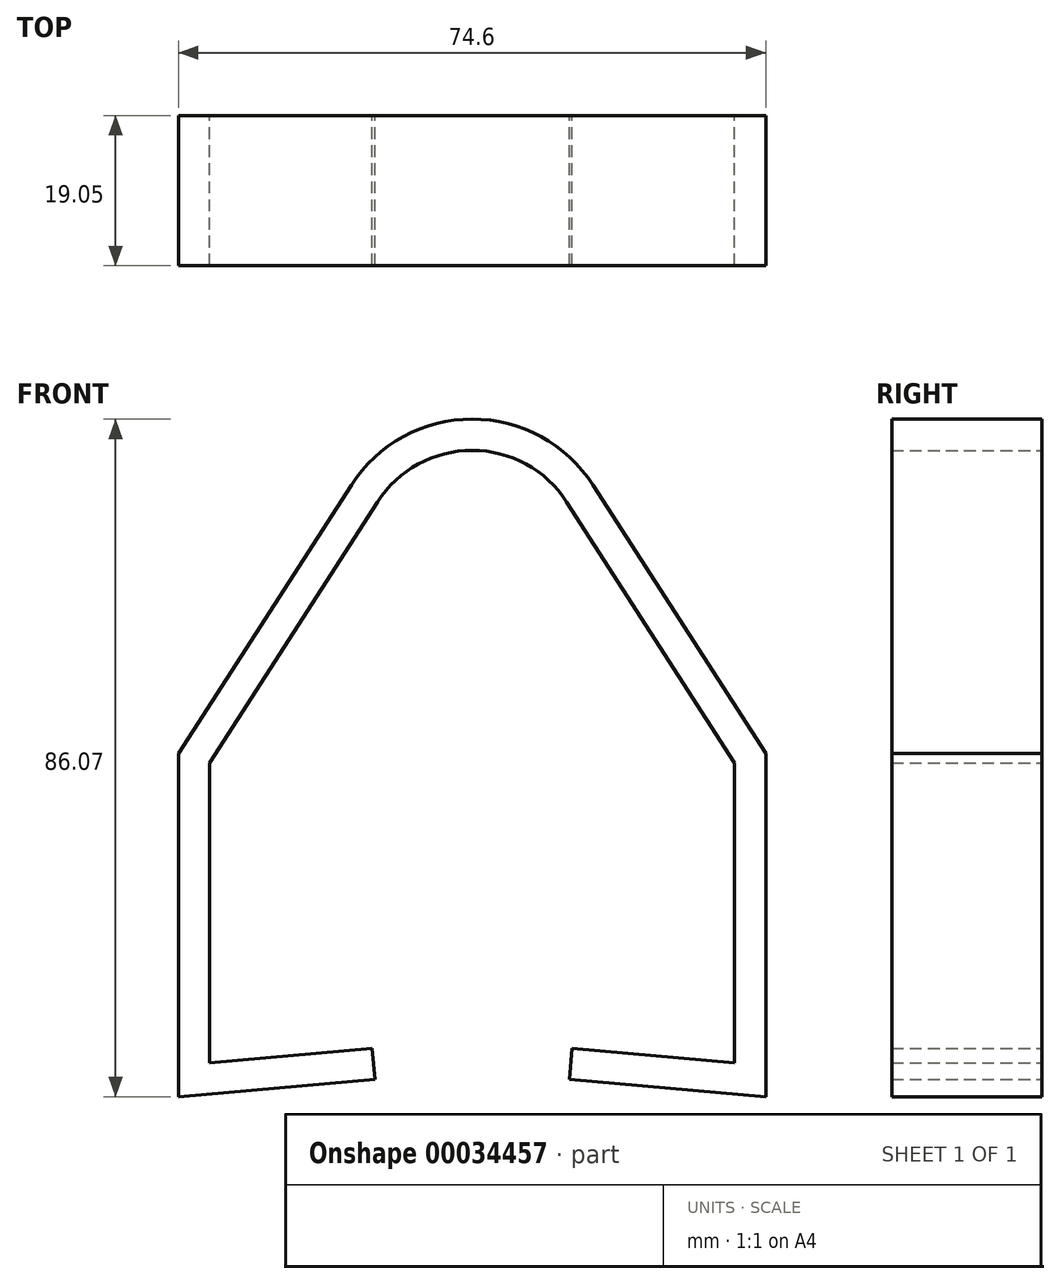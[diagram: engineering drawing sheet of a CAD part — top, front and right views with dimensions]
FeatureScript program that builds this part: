
annotation { "Feature Type Name" : "Feature", "Feature Type Description" : "" }
export const myFeature = defineFeature(function(context is Context, id is Id, definition is map)
    precondition{}
    {
        {
            var Q0;
            Q0=qCreatedBy(makeId("Front.planeOp"),FACE);
            var sketch = newSketch(context, id + "F0", { "sketchPlane" : qUnion([Q0])});
            skArc(sketch, "E0", {"start": v(12.01, 7.73) * mm, "mid": v(0, 14.29) * mm, "end": v(-12.01, 7.73) * mm});
            skLineSegment(sketch, "E1", {"start": v(0, 0) * mm, "end": v(0, -56.9) * mm, "construction": true});
            skLineSegment(sketch, "E2", {"start": v(12.01, 7.73) * mm, "end": v(33.34, -25.4) * mm});
            skLineSegment(sketch, "E3", {"start": v(33.34, -25.4) * mm, "end": v(33.34, -63.5) * mm});
            skLineSegment(sketch, "E4", {"start": v(33.34, -63.5) * mm, "end": v(12.7, -61.7) * mm});
            skLineSegment(sketch, "E5.0.MirrorCS", {"start": v(-12.01, 7.73) * mm, "end": v(-33.34, -25.4) * mm});
            skLineSegment(sketch, "E6.0.MirrorCS", {"start": v(-33.34, -25.4) * mm, "end": v(-33.34, -63.5) * mm});
            skLineSegment(sketch, "E7.0.MirrorCS", {"start": v(-33.34, -63.5) * mm, "end": v(-12.7, -61.7) * mm});
            skLineSegment(sketch, "E8.0", {"start": v(-37.3, -67.82) * mm, "end": v(-12.35, -65.64) * mm});
            skLineSegment(sketch, "E8.1", {"start": v(-37.3, -24.24) * mm, "end": v(-37.3, -67.82) * mm});
            skLineSegment(sketch, "E8.2", {"start": v(-15.35, 9.88) * mm, "end": v(-37.3, -24.24) * mm});
            skArc(sketch, "E8.3", {"start": v(15.35, 9.88) * mm, "mid": v(0, 18.25) * mm, "end": v(-15.35, 9.88) * mm});
            skLineSegment(sketch, "E8.4", {"start": v(15.35, 9.88) * mm, "end": v(37.3, -24.24) * mm});
            skLineSegment(sketch, "E8.5", {"start": v(37.3, -24.24) * mm, "end": v(37.3, -67.82) * mm});
            skLineSegment(sketch, "E8.6", {"start": v(37.3, -67.82) * mm, "end": v(12.35, -65.64) * mm});
            skLineSegment(sketch, "E9", {"start": v(12.7, -61.7) * mm, "end": v(12.35, -65.64) * mm});
            skLineSegment(sketch, "E10.0.MirrorCS", {"start": v(-12.7, -61.7) * mm, "end": v(-12.35, -65.64) * mm});
            skSolve(sketch);
        }
        {
            var Q0;
            Q0=qSketchRegion(id+"F0",true);
            extrude(context, id + "F1", {"entities" : qUnion([Q0]), "depth" : 19.05 * mm});
        }
    });
